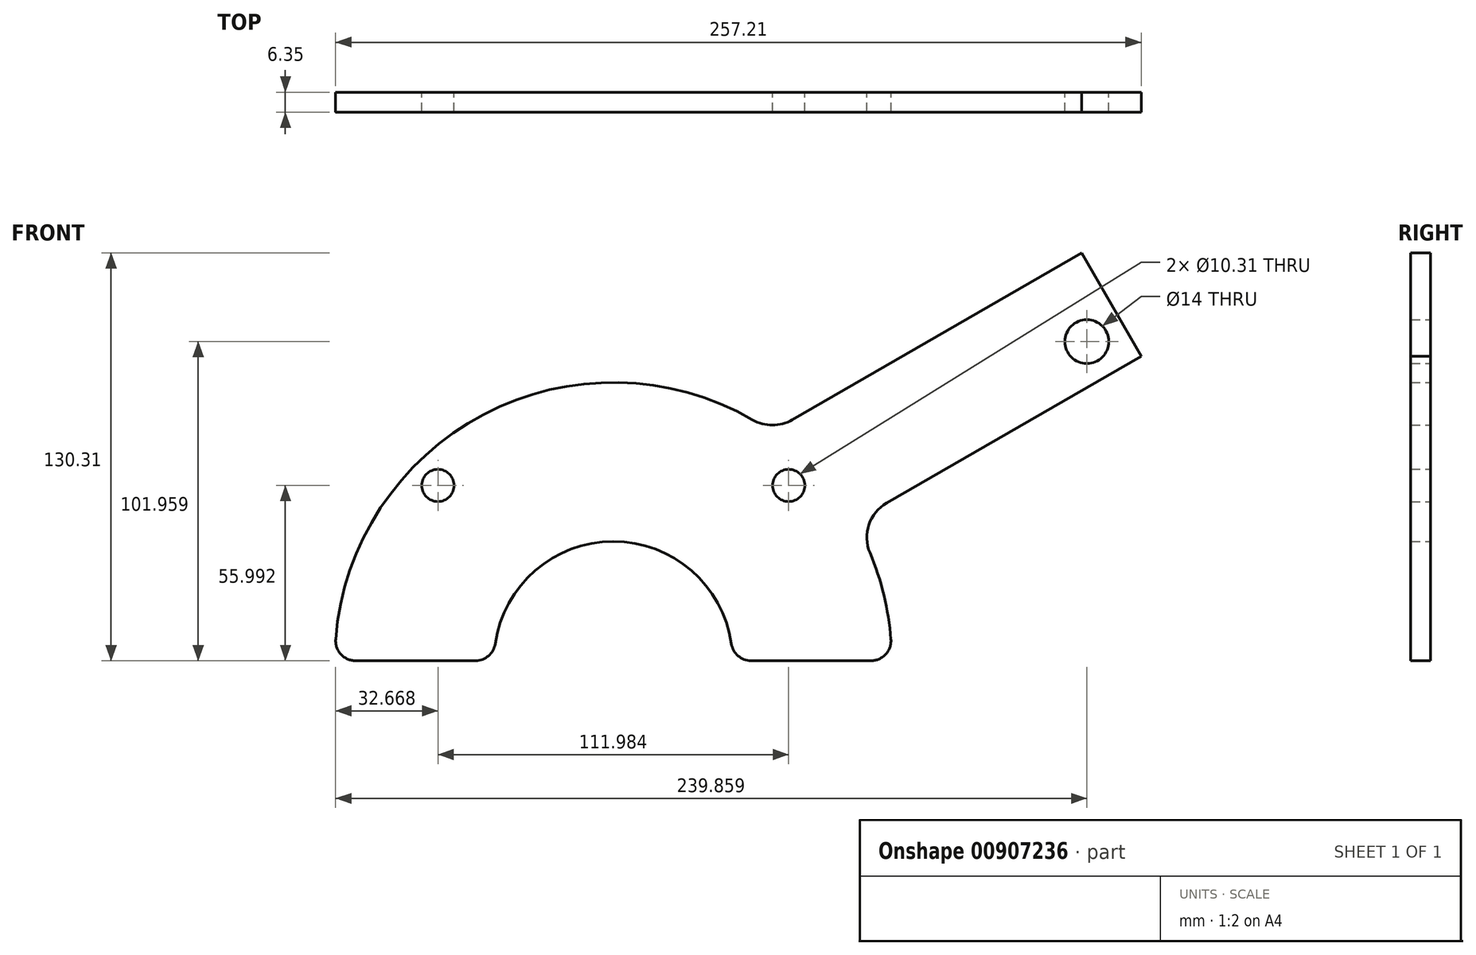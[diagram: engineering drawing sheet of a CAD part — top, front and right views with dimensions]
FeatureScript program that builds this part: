
annotation { "Feature Type Name" : "Feature", "Feature Type Description" : "" }
export const myFeature = defineFeature(function(context is Context, id is Id, definition is map)
    precondition{}
    {
        {
            var Q0;
            Q0=qCreatedBy(makeId("Front.planeOp"),FACE);
            var sketch = newSketch(context, id + "F0", { "sketchPlane" : qUnion([Q0])});
            skArc(sketch, "E0", {"start": v(88.9, 0) * mm, "mid": v(85.87, 23) * mm, "end": v(76.99, 44.45) * mm});
            skArc(sketch, "E1", {"start": v(38.1, 0) * mm, "mid": v(0, 38.1) * mm, "end": v(-38.1, 0) * mm});
            skLineSegment(sketch, "E2", {"start": v(-88.9, 0) * mm, "end": v(-38.1, 0) * mm});
            skLineSegment(sketch, "E3.trimOffspring", {"start": v(38.1, 0) * mm, "end": v(88.9, 0) * mm});
            skLineSegment(sketch, "E4", {"start": v(0, 0) * mm, "end": v(76.99, 44.45) * mm, "construction": true});
            skLineSegment(sketch, "E5", {"start": v(76.99, 44.45) * mm, "end": v(141.05, 81.44) * mm});
            skLineSegment(sketch, "E6", {"start": v(141.05, 81.44) * mm, "end": v(122, 114.43) * mm, "construction": true});
            skLineSegment(sketch, "E7", {"start": v(122, 114.43) * mm, "end": v(50.51, 73.16) * mm});
            skArc(sketch, "E8.trimOffspring", {"start": v(50.51, 73.16) * mm, "mid": v(-41.3, 78.72) * mm, "end": v(-88.9, 0) * mm});
            skLineSegment(sketch, "E9", {"start": v(122, 114.43) * mm, "end": v(149.5, 130.3) * mm});
            skLineSegment(sketch, "E10", {"start": v(149.5, 130.3) * mm, "end": v(168.55, 97.31) * mm});
            skLineSegment(sketch, "E11", {"start": v(168.55, 97.31) * mm, "end": v(141.05, 81.44) * mm});
            skSolve(sketch);
        }
        {
            var Q0;
            Q0=qSketchRegion(id+"F0",true);
            extrude(context, id + "F1", {"entities" : qUnion([Q0]), "depth" : 6.35 * mm, "offsetDistance" : 25.4 * mm});
        }
        {
            var Q0;
            Q0=makeQuery(id+"F1.opExtrude","CAP_FACE",FACE,{"disambiguationData":[OSD([sQuery(id+"F0.wireOp",EDGE,"E0"),sQuery(id+"F0.wireOp",EDGE,"E1")])],"isStart":false});
            var sketch = newSketch(context, id + "F2", { "sketchPlane" : qUnion([Q0])});
            skLineSegment(sketch, "E12", {"start": v(0, 0) * mm, "end": v(-62.86, 62.86) * mm, "construction": true});
            skPoint(sketch, "E13.center", {"position": v(0, 0) * mm});
            skLineSegment(sketch, "E14", {"start": v(0, 0) * mm, "end": v(62.86, 62.86) * mm, "construction": true});
            skPoint(sketch, "E15", {"position": v(-62.86, 62.86) * mm});
            skPoint(sketch, "E16", {"position": v(62.86, 62.86) * mm});
            skCircle(sketch, "E17", {"center": v(-56, 56) * mm, "radius": 7 * mm});
            skCircle(sketch, "E18", {"center": v(56, 56) * mm, "radius": 7 * mm});
            skSolve(sketch);
        }
        {
            var Q0;
            Q0=sQuery(id+"F2.wireOp",VERTEX,"E17.center");
            var Q1;
            Q1=sQuery(id+"F2.wireOp",VERTEX,"E18.center");
            var Q2;
            Q2=sQuery(id+"F2.wireOp",VERTEX,"63c57d3f-0896-44f0-a177-1cb718a14314");
            var Q3;
            Q3=sQuery(id+"F2.wireOp",VERTEX,"531b54bc-60c9-4a52-ae1a-907c0e3ef8af");
            var Q4;
            Q4=makeQuery(id+"F1.opExtrude","SWEPT_BODY",BODY,{"disambiguationData":[OSD([sQuery(id+"F0.wireOp",EDGE,"E0"),sQuery(id+"F0.wireOp",EDGE,"E1")])]});
            hole(context, id + "F3", {"style" : HoleStyle.SIMPLE, "endStyle" : HoleEndStyle.THROUGH, "standardTappedOrClearance" : lookupTablePath({ "fit" : "Normal (ASME)", "standard" : "ANSI", "size" : "3/8", "type" : "Clearance" }), "standardBlindInLast" : lookupTablePath({ "fit" : "Normal", "standard" : "ANSI", "engagement" : "75%", "pitch" : "16 tpi", "size" : "3/8", "type" : "Clearance & tapped" }), "holeDiameter" : 10.3 * mm, "majorDiameter" : 9.52 * mm, "isTappedThrough" : true, "tappedDepth" : 8.47 * mm, "tapClearance" : 3, "locations" : qUnion([Q0, Q1, Q2, Q3]), "scope" : qUnion([Q4]), "startStyle" : HoleStartStyle.SKETCH});
        }
        {
            var Q0;
            Q0=makeQuery(id+"F1.opExtrude","SWEPT_EDGE",EDGE,{"disambiguationData":[OSD([sQuery(id+"F0.wireOp",EDGE,"E7"),sQuery(id+"F0.wireOp",EDGE,"E8.trimOffspring")])]});
            var Q1;
            Q1=makeQuery(id+"F1.opExtrude","SWEPT_EDGE",EDGE,{"disambiguationData":[OSD([sQuery(id+"F0.wireOp",EDGE,"E0"),sQuery(id+"F0.wireOp",EDGE,"E5")])]});
            fillet(context, id + "F4", {"entities" : qUnion([Q0, Q1]), "radius" : 12.7 * mm, "tangentPropagation" : true, "allowEdgeOverflow" : false});
        }
        {
            var Q0;
            Q0=makeQuery(id+"F1.opExtrude","SWEPT_EDGE",EDGE,{"disambiguationData":[OSD([sQuery(id+"F0.wireOp",EDGE,"E0"),sQuery(id+"F0.wireOp",EDGE,"E3.trimOffspring")])]});
            var Q1;
            Q1=makeQuery(id+"F1.opExtrude","SWEPT_EDGE",EDGE,{"disambiguationData":[OSD([sQuery(id+"F0.wireOp",EDGE,"E1"),sQuery(id+"F0.wireOp",EDGE,"E3.trimOffspring")])]});
            var Q2;
            Q2=makeQuery(id+"F1.opExtrude","SWEPT_EDGE",EDGE,{"disambiguationData":[OSD([sQuery(id+"F0.wireOp",EDGE,"E1"),sQuery(id+"F0.wireOp",EDGE,"E2")])]});
            var Q3;
            Q3=makeQuery(id+"F1.opExtrude","SWEPT_EDGE",EDGE,{"disambiguationData":[OSD([sQuery(id+"F0.wireOp",EDGE,"E2"),sQuery(id+"F0.wireOp",EDGE,"E8.trimOffspring")])]});
            fillet(context, id + "F5", {"entities" : qUnion([Q0, Q1, Q2, Q3]), "radius" : 6.35 * mm, "tangentPropagation" : true, "allowEdgeOverflow" : false});
        }
        {
            var Q0;
            Q0=makeQuery(id+"F1.opExtrude","CAP_FACE",FACE,{"disambiguationData":[OSD([sQuery(id+"F0.wireOp",EDGE,"E0"),sQuery(id+"F0.wireOp",EDGE,"E1"),sQuery(id+"F0.wireOp",EDGE,"E2"),sQuery(id+"F0.wireOp",EDGE,"E3.trimOffspring"),sQuery(id+"F0.wireOp",EDGE,"E5"),sQuery(id+"F0.wireOp",EDGE,"E7"),sQuery(id+"F0.wireOp",EDGE,"E8.trimOffspring"),sQuery(id+"F0.wireOp",EDGE,"E9"),sQuery(id+"F0.wireOp",EDGE,"E10"),sQuery(id+"F0.wireOp",EDGE,"E11")])],"isStart":false});
            var sketch = newSketch(context, id + "F6", { "sketchPlane" : qUnion([Q0])});
            skPoint(sketch, "E19", {"position": v(151.2, 101.96) * mm});
            skSolve(sketch);
        }
        {
            var Q0;
            Q0=sQuery(id+"F6.wireOp",VERTEX,"E19");
            var Q1;
            Q1=makeQuery(id+"F1.opExtrude","SWEPT_BODY",BODY,{"disambiguationData":[OSD([sQuery(id+"F0.wireOp",EDGE,"E0"),sQuery(id+"F0.wireOp",EDGE,"E1"),sQuery(id+"F0.wireOp",EDGE,"E2"),sQuery(id+"F0.wireOp",EDGE,"E3.trimOffspring"),sQuery(id+"F0.wireOp",EDGE,"E5"),sQuery(id+"F0.wireOp",EDGE,"E7"),sQuery(id+"F0.wireOp",EDGE,"E8.trimOffspring"),sQuery(id+"F0.wireOp",EDGE,"E9"),sQuery(id+"F0.wireOp",EDGE,"E10"),sQuery(id+"F0.wireOp",EDGE,"E11")])]});
            hole(context, id + "F7", {"style" : HoleStyle.SIMPLE, "endStyle" : HoleEndStyle.THROUGH, "standardTappedOrClearance" : lookupTablePath({ "standard" : "ISO", "size" : "14", "type" : "Drilled" }), "standardBlindInLast" : lookupTablePath({ "standard" : "ISO", "size" : "14", "type" : "Drilled" }), "holeDiameter" : 14 * mm, "majorDiameter" : 6.35 * mm, "isTappedThrough" : true, "tappedDepth" : 8.47 * mm, "tapClearance" : 3, "locations" : qUnion([Q0]), "scope" : qUnion([Q1]), "startStyle" : HoleStartStyle.SKETCH});
        }
    });
